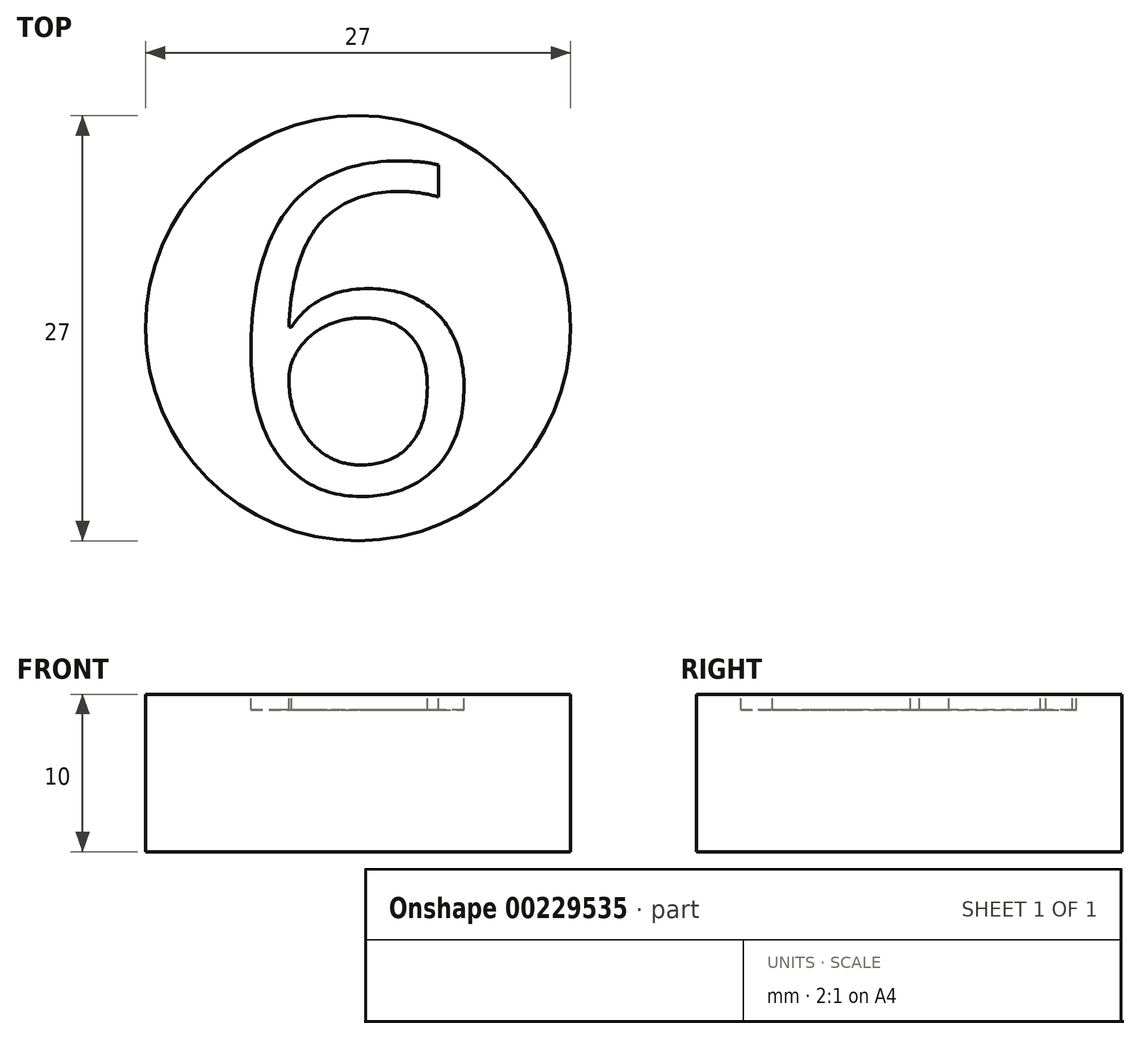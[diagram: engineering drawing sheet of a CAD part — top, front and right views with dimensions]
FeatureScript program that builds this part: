
annotation { "Feature Type Name" : "Feature", "Feature Type Description" : "" }
export const myFeature = defineFeature(function(context is Context, id is Id, definition is map)
    precondition{}
    {
        {
            var Q0;
            Q0=qCreatedBy(makeId("Top.planeOp"),FACE);
            var sketch = newSketch(context, id + "F0", { "sketchPlane" : qUnion([Q0])});
            skCircle(sketch, "E0", {"center": v(0, 0) * mm, "radius": 13.5 * mm});
            skSolve(sketch);
        }
        {
            var Q0;
            Q0=makeQuery(id+"F0.imprint","IMPRINT",FACE,{"disambiguationData":[TD([[makeQuery(id+"F0.imprint","IMPRINT",EDGE,{"derivedFrom":sQuery(id+"F0.wireOp",EDGE,"E0")}),1.0]])]});
            extrude(context, id + "F1", {"entities" : qUnion([Q0]), "depth" : 10 * mm});
        }
        {
            var Q0;
            Q0=makeQuery(id+"F1.opExtrude","CAP_FACE",FACE,{"disambiguationData":[OSD([sQuery(id+"F0.wireOp",EDGE,"E0")])],"isStart":false});
            var sketch = newSketch(context, id + "F2", { "sketchPlane" : qUnion([Q0])});
            skText(sketch, "E1", { "text": "6", "fontName": "OpenSans-Regular.ttf"});
            const initialGuessF2  = {"E1": [-0.00846, -0.0104, 1, 0, 0.02091]};
            skSetInitialGuess(sketch, initialGuessF2);
            skSolve(sketch);
        }
        {
            var Q0;
            Q0=makeQuery(id+"F2.imprint","IMPRINT",FACE,{"disambiguationData":[TD([[makeQuery(id+"F2.imprint","IMPRINT",EDGE,{"derivedFrom":sQuery(id+"F2.wireOp",EDGE,"E1.sketch_text.stroke-0")}),-1.0]])]});
            extrude(context, id + "F3", {"entities" : qUnion([Q0]), "operationType" : NewBodyOperationType.REMOVE, "oppositeDirection" : true, "depth" : 1 * mm});
        }
    });
